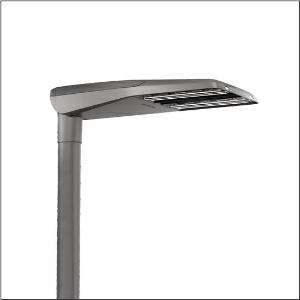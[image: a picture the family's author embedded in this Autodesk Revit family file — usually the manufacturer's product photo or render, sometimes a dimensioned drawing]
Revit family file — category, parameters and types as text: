
# Revit family: streetlight_sl_11_iq_midi___st1_2p1_0_5xc3g41e08me_f4ca
name_source: partatom
category: Lighting Fixtures
units: mm (PartAtom-declared; Revit-internal decimal feet)

## family parameters
Cut with Voids When Loaded = No
Host = Face
Light Source = No
Part Type = Normal
Room Calculation Point = No
Round Connector Dimension = Use Diameter
Shared = No

## types (1)
- --- (1 x LED, 18520 lm, 121.7 W, 4000K)
    Apparent Load = 122 VA
    CIE Flux Codes = 31 68 95 100 100
    Color Rendering = 70
    Color Temperature = 4000K
    Default Elevation = 1800 mm
    Description = Streetlight SL 11 iQ midi, mast luminaire, primary light control with 3 zone facetted reflector, of plastic, silver coated, highly specular, primary optical cover: cover, of PMMA, transparent, light distribution: ST1.2P1.0, light emission: direct distribution, primary light characteristic: asymmetric, installation type: post-top, side-entry, lamps: LED, High Power LED, rated values: 18.520lm | 121,7W | 152,2lm/W (begin service life); end service life: 18.520lm | 129W; at 50% lumin. flux: 9.260lm | 56,2W | 164,8lm/W, colour temperature: 4000K, colour rendering: CRI > 70, light colour: 740, light setting 1 begin service life: 100% | 18.520lm | 121,7W | 152,2lm/W | 4.000K, light setting 1 end service life: 129W, further light settings possible, control: optimised constant luminous flux control (CLO 2.0), Desk-Remote (wireless, voltage-free reading and setting of iQ features in the workshop via application-optimized NFC function/RFID function), Light-Fading, Smart-Wire, Night-Set, Lumen-Switch, Temp-Guard, Auto-Match, with cable H07RN-F 5x 1.5mm², mains connection: 230..240V, AC, 50/60Hz, connection cable pre-assembled, cable length: 12,5m, luminaire housing, of diecast aluminium, powder-coated, Siteco® metallic grey (DB 702S), please order mast flange separately, inclination adjustable without tools: 0°, 5°, 10°, 15° (post-top) | 0°, -5°, -10°, -15° (side-entry), sealing non-destructively replaceable, multi-level sealing system, length: 780mm, width: 376mm, height: 118mm, mast flange for spigot size: 42mm (side-entry): 5XC10008XM4, 60/48mm (side-entry/post-top): 5XC10108XM2, 76/60mm (side-entry/post-top): 5XC10108XM1, equipment: Power, protection rating (complete): IP66, insulation class (complete): insulation class II (safety insulation), certification: CE, ENEC, ENEC+, VDE, impact resistance: IK10, permissible operating ambient temperature for outdoor applications: -25..+50°C, standard-compliant lighting for roads and squares, Environmental Product Declaration (EPD) tested and certified by an independent institute, packaging unit: 1 piece

Light Distribution: ST1.2P1.0
    Height = 118 mm
    Lamp = 1 x LED
    Lamp Light Flux = 18520 lm
    Lamp Power = 121.7 W
    Lamp count = 1
    Length = 780 mm
    Luminous efficacy = 152 lm/W
    Manufacturer = Siteco
    ModVariant = No
    Model = 5XC3G41E08ME
    Number of Poles = 1
    OnlyDefault = Yes
    Power Factor = 1
    Product Name = Streetlight SL 11 iQ midi | ST1.2P1.0
    Product group = mast luminaire | pylon top
    ProductGroupID = 6100
    Protection Class = Protection class II
    Protection Degree = IP 66
    RLX_Detail_Level = 1
    RLX_Emergency_Light_Flux = 0 lm
    RLX_Emergency_Type = 0
    RLX_Emergency_Type_DB = No
    RlxData = <blob elided: 71021 chars, md5=47ad96fd>
    Socket = socket
    Standby Power = 0 W
    System Light Flux = 18520 lm
    System Power = 122 W
    Type Comments = factory setting: luminous flux: 100 % | dim-lin: 254 | 544 mA
    Type Image = l_1005960.jpg
    URL = http://relux.com
    VarID = @adj_046515
    Voltage = 0 V
    Weight = 0.00 kg
    Width = 376 mm

## geometry (parser evidence)
native form markers: Blend x4, Sweep x8
no freeform markers — native parametric forms only
